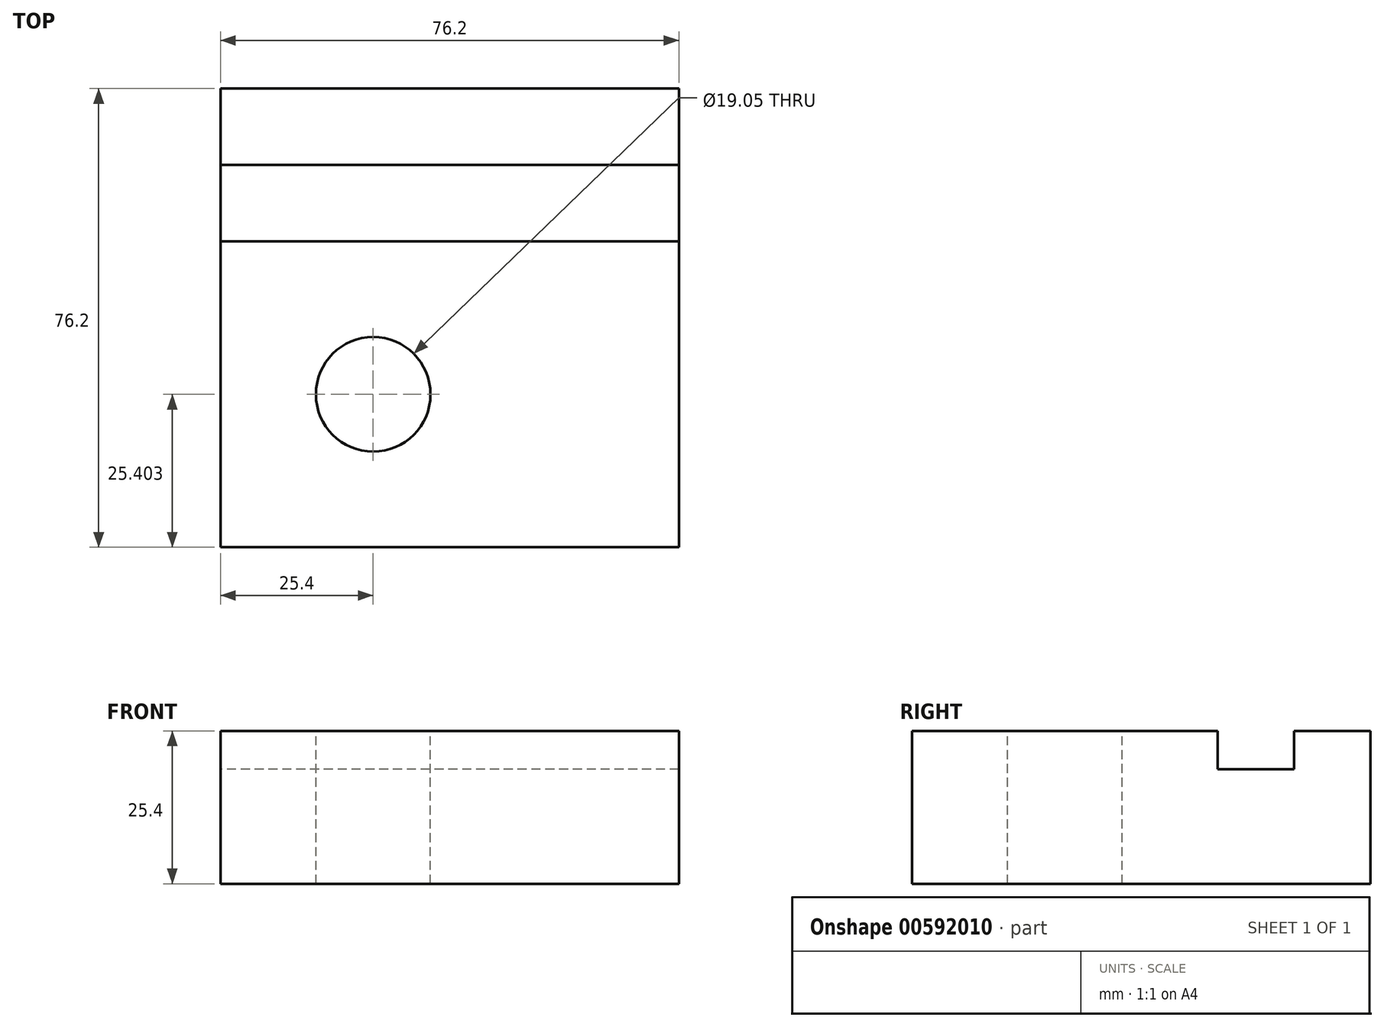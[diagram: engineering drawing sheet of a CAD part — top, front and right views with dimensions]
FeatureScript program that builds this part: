
annotation { "Feature Type Name" : "Feature", "Feature Type Description" : "" }
export const myFeature = defineFeature(function(context is Context, id is Id, definition is map)
    precondition{}
    {
        {
            var Q0;
            Q0=qCreatedBy(makeId("Right.planeOp"),FACE);
            var sketch = newSketch(context, id + "F0", { "sketchPlane" : qUnion([Q0])});
            skLineSegment(sketch, "E0", {"start": v(-84.8, 27.8) * mm, "end": v(-84.8, 2.4) * mm});
            skLineSegment(sketch, "E1", {"start": v(-84.8, 2.4) * mm, "end": v(-8.6, 2.4) * mm});
            skLineSegment(sketch, "E2", {"start": v(-8.6, 2.4) * mm, "end": v(-8.6, 27.8) * mm});
            skLineSegment(sketch, "E3", {"start": v(-8.6, 27.8) * mm, "end": v(-21.3, 27.8) * mm});
            skLineSegment(sketch, "E4", {"start": v(-21.3, 27.8) * mm, "end": v(-21.3, 21.46) * mm});
            skLineSegment(sketch, "E5", {"start": v(-21.3, 21.46) * mm, "end": v(-34, 21.46) * mm});
            skLineSegment(sketch, "E6", {"start": v(-34, 21.46) * mm, "end": v(-34, 27.8) * mm});
            skLineSegment(sketch, "E7", {"start": v(-34, 27.8) * mm, "end": v(-84.8, 27.8) * mm});
            skSolve(sketch);
        }
        {
            var Q0;
            Q0=qSketchRegion(id+"F0",true);
            extrude(context, id + "F1", {"entities" : qUnion([Q0]), "depth" : 76.2 * mm, "offsetDistance" : 25.4 * mm});
        }
        {
            var Q0;
            Q0=makeQuery(id+"F1.opExtrude","SWEPT_FACE",FACE,{"disambiguationData":[OSD([sQuery(id+"F0.wireOp",EDGE,"E7")])]});
            var sketch = newSketch(context, id + "F2", { "sketchPlane" : qUnion([Q0])});
            skLineSegment(sketch, "E8", {"start": v(-16.59, -59.4) * mm, "end": v(42.65, -59.4) * mm, "construction": true});
            skLineSegment(sketch, "E9", {"start": v(25.4, -105.43) * mm, "end": v(25.4, -46.23) * mm, "construction": true});
            skCircle(sketch, "E10", {"center": v(25.4, -59.4) * mm, "radius": 9.53 * mm});
            skSolve(sketch);
        }
        {
            var Q0;
            Q0=qSketchRegion(id+"F2",true);
            extrude(context, id + "F3", {"entities" : qUnion([Q0]), "operationType" : NewBodyOperationType.REMOVE, "endBound" : BoundingType.THROUGH_ALL, "oppositeDirection" : true, "depth" : 25.4 * mm, "offsetDistance" : 25.4 * mm});
        }
    });
